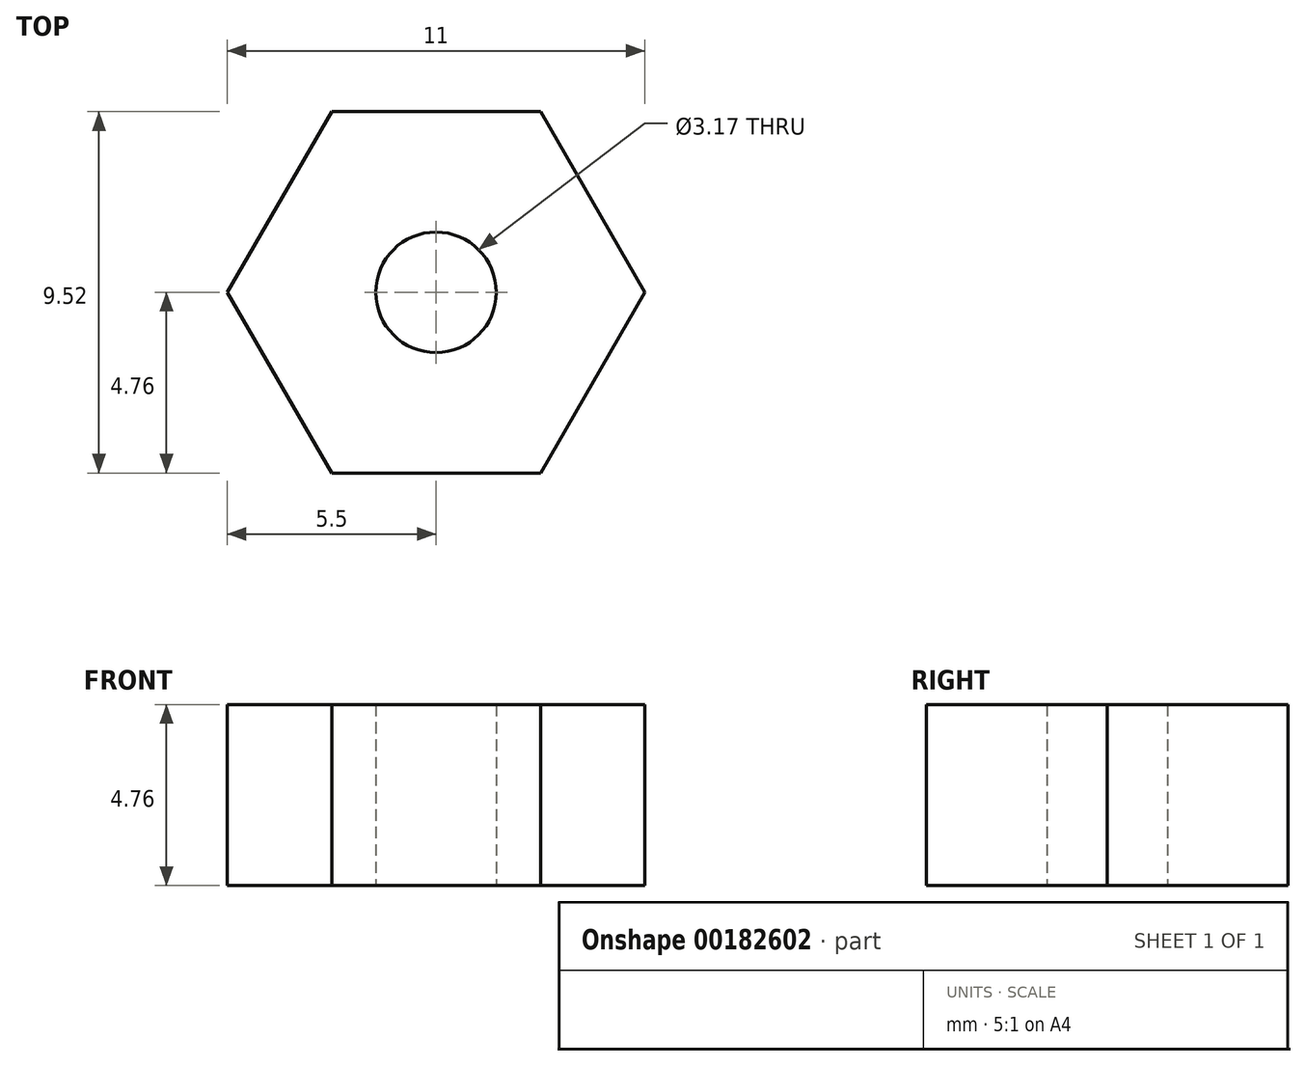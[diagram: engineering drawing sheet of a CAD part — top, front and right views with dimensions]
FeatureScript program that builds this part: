
annotation { "Feature Type Name" : "Feature", "Feature Type Description" : "" }
export const myFeature = defineFeature(function(context is Context, id is Id, definition is map)
    precondition{}
    {
        {
            var Q0;
            Q0=qCreatedBy(makeId("Top.planeOp"),FACE);
            var sketch = newSketch(context, id + "F0", { "sketchPlane" : qUnion([Q0])});
            skCircle(sketch, "E0.cCircle", {"center": v(0, 0) * mm, "radius": 4.76 * mm, "construction": true});
            skLineSegment(sketch, "E0.0", {"start": v(-2.75, 4.76) * mm, "end": v(2.75, 4.76) * mm});
            skLineSegment(sketch, "E0.1", {"start": v(2.75, 4.76) * mm, "end": v(5.5, 0) * mm});
            skLineSegment(sketch, "E0.2", {"start": v(5.5, 0) * mm, "end": v(2.75, -4.76) * mm});
            skLineSegment(sketch, "E0.3", {"start": v(2.75, -4.76) * mm, "end": v(-2.75, -4.76) * mm});
            skLineSegment(sketch, "E0.4", {"start": v(-2.75, -4.76) * mm, "end": v(-5.5, 0) * mm});
            skLineSegment(sketch, "E0.5", {"start": v(-5.5, 0) * mm, "end": v(-2.75, 4.76) * mm});
            skPoint(sketch, "E0.0.midPoint", {"position": v(0, 4.76) * mm});
            skCircle(sketch, "E1", {"center": v(0, 0) * mm, "radius": 1.59 * mm});
            skSolve(sketch);
        }
        {
            var Q0;
            Q0 = qSketchRegion(id + "F0", true);
            extrude(context, id + "F1", {"entities" : qUnion([Q0]), "depth" : 4.76 * mm});
        }
    });
